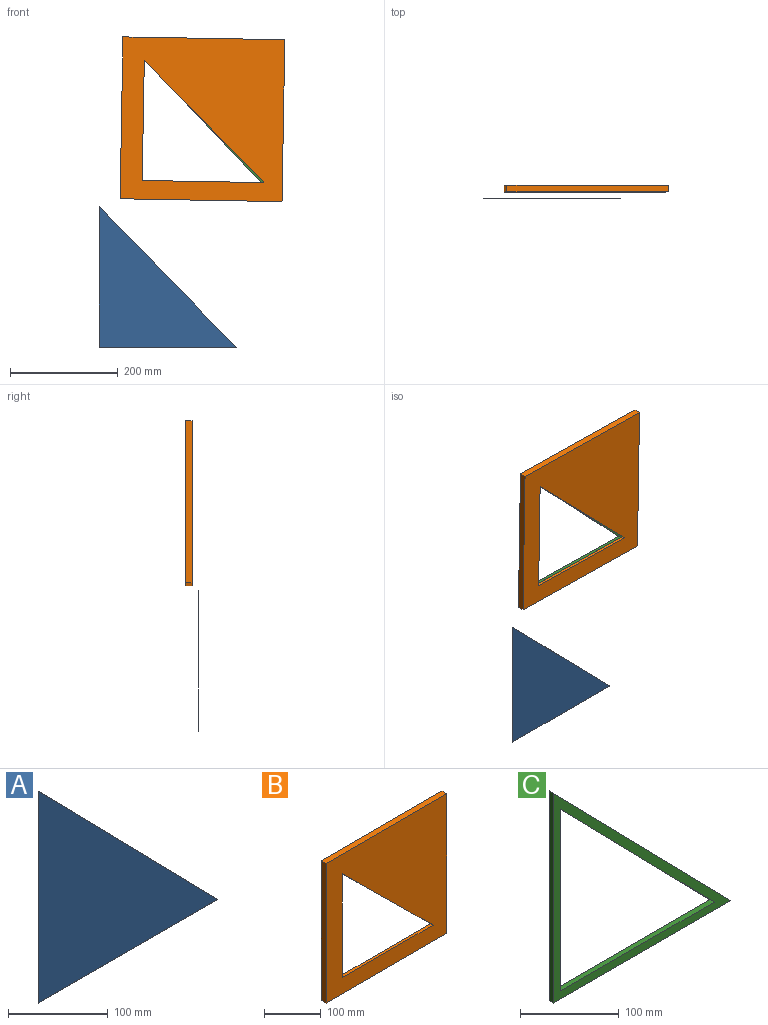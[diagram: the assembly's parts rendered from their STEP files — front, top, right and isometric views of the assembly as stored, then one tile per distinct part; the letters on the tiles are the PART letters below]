
ASSEMBLY  parts=3 mates=1
PART A: 5 faces, bbox 254x0.5x260.1 mm
  f0: plane 260.1x254.04mm, normal (0.72,0,0.7), area 181.8mm2, adj f1,f2,f3,f4
  f1: plane 260.1x0.5mm, normal (-1,0,0), area 130.1mm2, adj f0,f2,f3,f4
  f2: plane 254.04x0.5mm, normal (0,0,-1), area 127mm2, adj f0,f1,f3,f4
  f3: plane 260.1x254.04mm, normal (0,-1,0), area 33039mm2, adj f0,f1,f2
  f4: plane 260.1x254.04mm, normal (0,1,0), area 33039mm2, adj f0,f1,f2
PART B: 13 faces, bbox 300x12x300 mm
  f0: plane 300x300mm, normal (0,1,0), area 56570.8mm2, adj f5,f6,f7,f8,f9,f10,f11
  f1: plane 225.76x223.1mm, normal (-0.7,0,-0.71), area 1904.4mm2, adj f2,f3,f4,f12
  f2: plane 223.1x6mm, normal (1,0,0), area 1338.6mm2, adj f1,f3,f4,f12
  f3: plane 225.76x6mm, normal (0,0,1), area 1354.6mm2, adj f1,f2,f4,f12
  f4: plane 300x300mm, normal (0,-1,0), area 64816.3mm2, adj f1,f2,f3,f5,f6,f7,f8
  f5: plane 300x12mm, normal (-1,0,0), area 3600mm2, adj f0,f4,f6,f8
  f6: plane 300x12mm, normal (0,0,-1), area 3600mm2, adj f0,f4,f5,f7
  f7: plane 300x12mm, normal (1,0,0), area 3600mm2, adj f0,f4,f6,f8
  f8: plane 300x12mm, normal (0,0,1), area 3600mm2, adj f0,f4,f5,f7
  f9: plane 260.1x6mm, normal (0,0,1), area 1560.6mm2, adj f0,f10,f11,f12
  f10: plane 257.04x6mm, normal (1,0,0), area 1542.3mm2, adj f0,f9,f11,f12
  f11: plane 260.1x257.04mm, normal (-0.7,0,-0.71), area 2194.1mm2, adj f0,f9,f10,f12
  f12: plane 260.1x257.04mm, normal (0,1,0), area 8245.5mm2, adj f1,f2,f3,f9,f10,f11
PART C: 8 faces, bbox 254x6x260.1 mm
  f0: plane 260.1x254.04mm, normal (0.72,0,0.7), area 2181.5mm2, adj f1,f5,f6,f7
  f1: plane 260.1x6mm, normal (-1,0,0), area 1560.6mm2, adj f0,f5,f6,f7
  f2: plane 225.55x220.3mm, normal (-0.72,0,-0.7), area 1891.7mm2, adj f3,f4,f6,f7
  f3: plane 220.3x6mm, normal (0,0,1), area 1321.8mm2, adj f2,f4,f6,f7
  f4: plane 225.55x6mm, normal (1,0,0), area 1353.3mm2, adj f2,f3,f6,f7
  f5: plane 254.04x6mm, normal (0,0,-1), area 1524.3mm2, adj f0,f1,f6,f7
  f6: plane 260.1x254.04mm, normal (0,-1,0), area 8194.4mm2, adj f0,f1,f2,f3,f4,f5
  f7: plane 260.1x254.04mm, normal (0,1,0), area 8194.4mm2, adj f0,f1,f2,f3,f4,f5
PLACE A t=(58.92,3.69,-36.36)mm
PLACE B rot(axis=(0,1,0),1deg) t=(97.7,26.92,238.52)mm
PLACE C rot(axis=(0,1,0),1deg) t=(128.42,26.92,262.63)mm
MATE fastened B.f9 <-> C.f5  axis (0.02,0,1) through (128.42,26.92,262.63)mm
